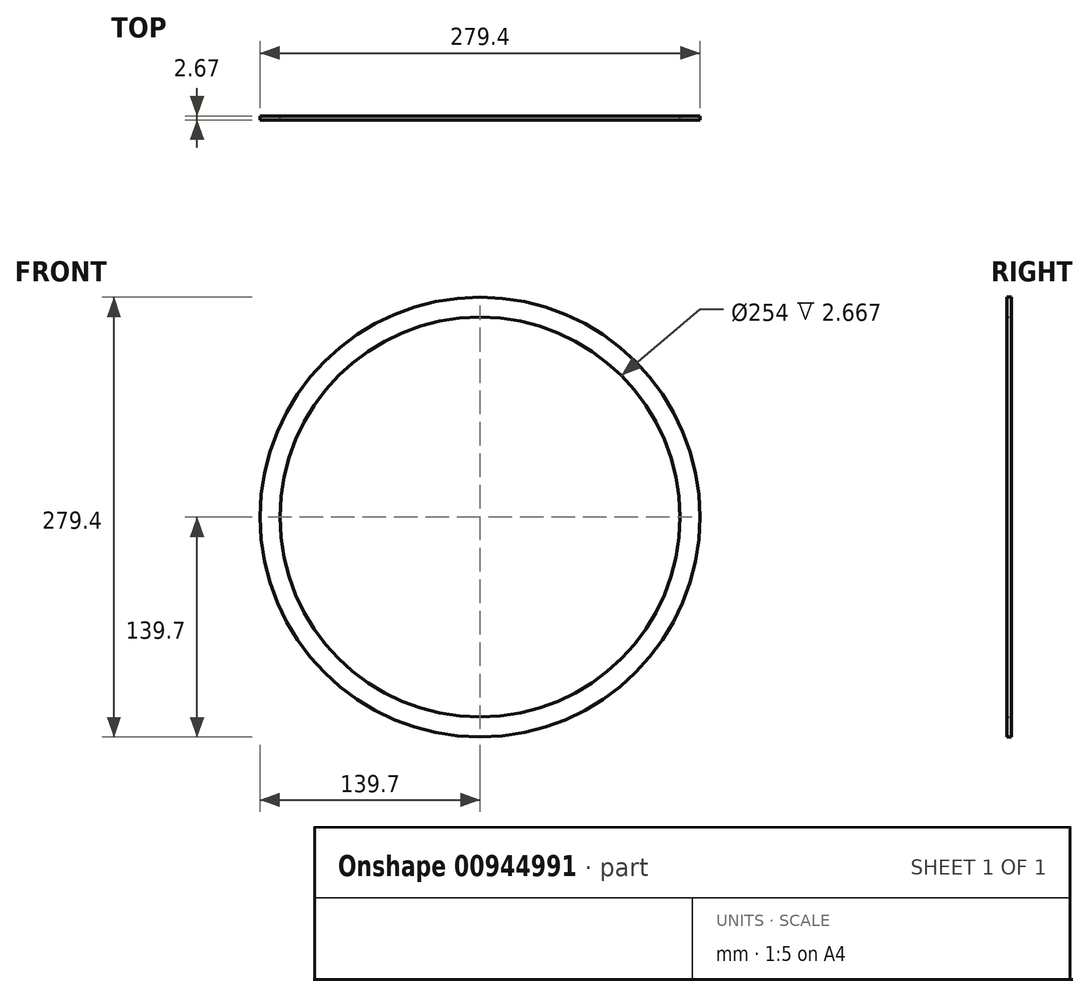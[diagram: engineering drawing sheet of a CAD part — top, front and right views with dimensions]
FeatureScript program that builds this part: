
annotation { "Feature Type Name" : "Feature", "Feature Type Description" : "" }
export const myFeature = defineFeature(function(context is Context, id is Id, definition is map)
    precondition{}
    {
        {
            var Q0;
            Q0=qCreatedBy(makeId("Front.planeOp"),FACE);
            var sketch = newSketch(context, id + "F0", { "sketchPlane" : qUnion([Q0])});
            skCircle(sketch, "E0", {"center": v(0, 0) * mm, "radius": 139.7 * mm});
            skCircle(sketch, "E1", {"center": v(0, 0) * mm, "radius": 127 * mm});
            skSolve(sketch);
        }
        {
            var Q0;
            Q0 = qSketchRegion(id + "F0", true);
            extrude(context, id + "F1", {"entities" : qUnion([Q0]), "depth" : 2.67 * mm, "offsetDistance" : 25.4 * mm});
        }
    });
